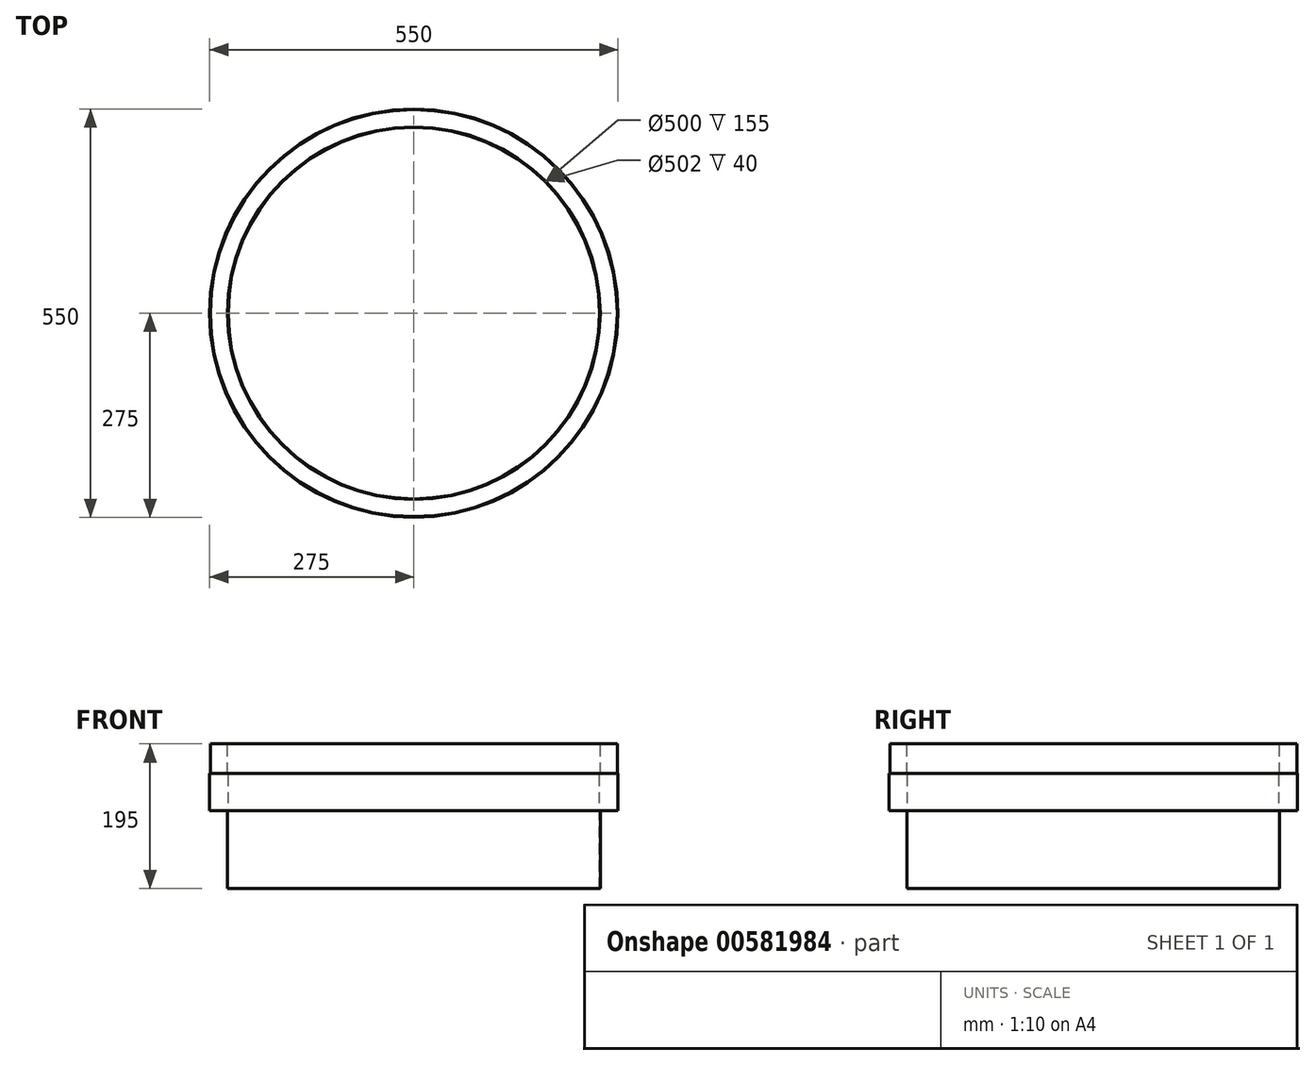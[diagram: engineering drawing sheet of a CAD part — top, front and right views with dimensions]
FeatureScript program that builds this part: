
annotation { "Feature Type Name" : "Feature", "Feature Type Description" : "" }
export const myFeature = defineFeature(function(context is Context, id is Id, definition is map)
    precondition{}
    {
        {
            var Q0;
            Q0=qCreatedBy(makeId("Front.planeOp"),FACE);
            var sketch = newSketch(context, id + "F0", { "sketchPlane" : qUnion([Q0])});
            skLineSegment(sketch, "E0", {"start": v(0, 710.75) * mm, "end": v(0, -704.58) * mm, "construction": true});
            skLineSegment(sketch, "E1", {"start": v(-250, 295.65) * mm, "end": v(-250, 410.65) * mm});
            skLineSegment(sketch, "E2", {"start": v(-250, 410.65) * mm, "end": v(-251, 410.65) * mm});
            skLineSegment(sketch, "E3", {"start": v(-274, 410.65) * mm, "end": v(-275, 410.65) * mm});
            skLineSegment(sketch, "E4", {"start": v(-275, 410.65) * mm, "end": v(-275, 360.65) * mm});
            skLineSegment(sketch, "E5", {"start": v(-275, 360.65) * mm, "end": v(-251, 360.65) * mm});
            skLineSegment(sketch, "E6", {"start": v(-251, 360.65) * mm, "end": v(-251, 295.65) * mm});
            skLineSegment(sketch, "E7", {"start": v(-274, 450.65) * mm, "end": v(-274, 410.65) * mm});
            skLineSegment(sketch, "E8", {"start": v(-274, 450.65) * mm, "end": v(-251, 450.65) * mm});
            skLineSegment(sketch, "E9", {"start": v(-251, 410.65) * mm, "end": v(-251, 450.65) * mm});
            skLineSegment(sketch, "E10", {"start": v(-250, 295.65) * mm, "end": v(-250, 255.65) * mm});
            skLineSegment(sketch, "E11", {"start": v(-251, 295.65) * mm, "end": v(-251, 255.65) * mm});
            skLineSegment(sketch, "E12", {"start": v(-251, 255.65) * mm, "end": v(-250, 255.65) * mm});
            skSolve(sketch);
        }
        {
            var Q0;
            Q0=qSketchRegion(id+"F0",true);
            var Q1;
            Q1=sQuery(id+"F0.wireOp",EDGE,"E0");
            revolve(context, id + "F1", {"entities" : qUnion([Q0]), "axis" : qUnion([Q1]), "revolveType" : RevolveType.FULL});
        }
    });
